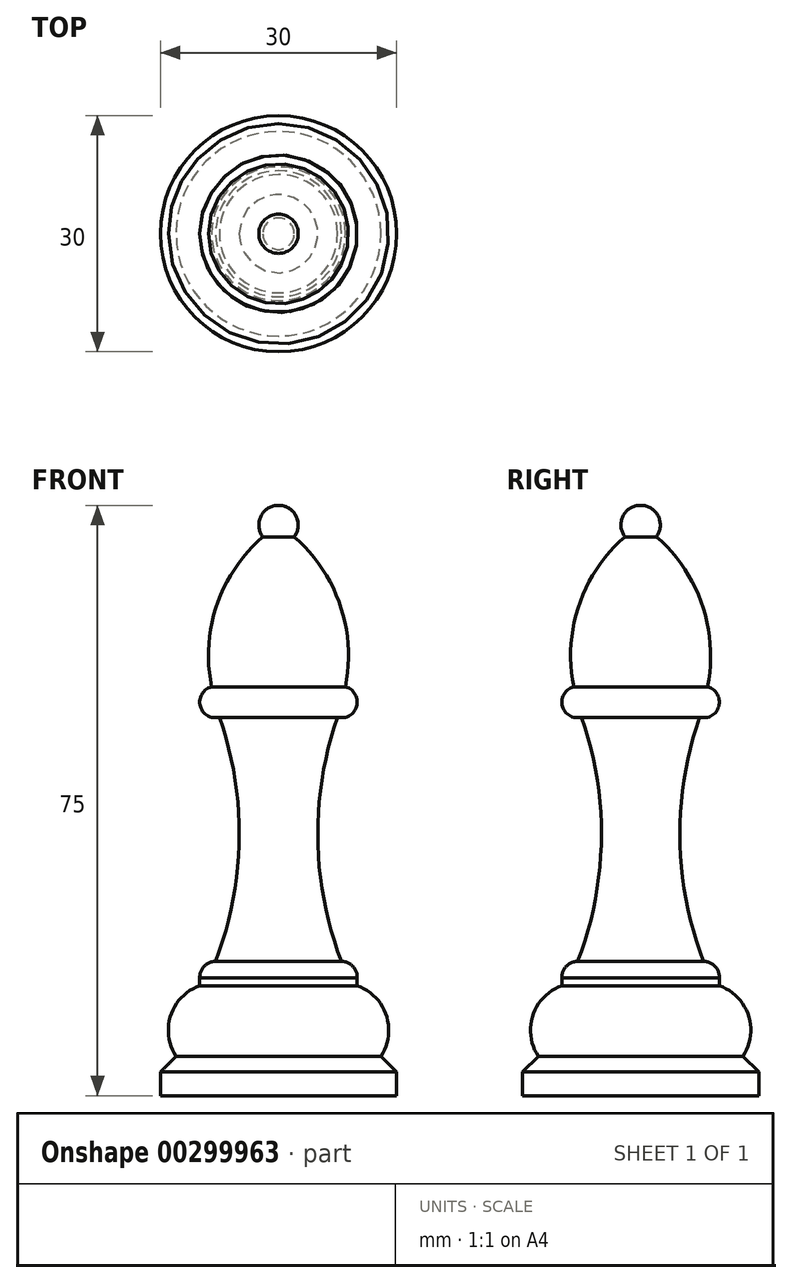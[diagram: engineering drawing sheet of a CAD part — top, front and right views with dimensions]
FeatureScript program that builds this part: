
annotation { "Feature Type Name" : "Feature", "Feature Type Description" : "" }
export const myFeature = defineFeature(function(context is Context, id is Id, definition is map)
    precondition{}
    {
        {
            var Q0;
            Q0=qCreatedBy(makeId("Front.planeOp"),FACE);
            var sketch = newSketch(context, id + "F0", { "sketchPlane" : qUnion([Q0])});
            skArc(sketch, "E0", {"start": v(2, -4) * mm, "mid": v(2.24, -1.38) * mm, "end": v(0, 0) * mm});
            skArc(sketch, "E1", {"start": v(8.5, -23.06) * mm, "mid": v(7.82, -12.65) * mm, "end": v(2, -4) * mm});
            skArc(sketch, "E2", {"start": v(8.5, -26.93) * mm, "mid": v(10, -25) * mm, "end": v(8.5, -23.06) * mm});
            skLineSegment(sketch, "E3", {"start": v(8.5, -26.93) * mm, "end": v(7.5, -26.93) * mm});
            skArc(sketch, "E4", {"start": v(7.5, -26.93) * mm, "mid": v(5, -42.49) * mm, "end": v(8, -57.95) * mm});
            skArc(sketch, "E5", {"start": v(10, -60.03) * mm, "mid": v(9.44, -58.57) * mm, "end": v(8, -57.95) * mm});
            skLineSegment(sketch, "E6", {"start": v(10, -60.03) * mm, "end": v(10, -61.03) * mm});
            skLineSegment(sketch, "E7", {"start": v(13, -70) * mm, "end": v(15, -72) * mm});
            skLineSegment(sketch, "E8", {"start": v(15, -72) * mm, "end": v(15, -75) * mm});
            skLineSegment(sketch, "E9", {"start": v(15, -75) * mm, "end": v(0, -75) * mm});
            skLineSegment(sketch, "E10", {"start": v(0, -75) * mm, "end": v(0, 0) * mm});
            skArc(sketch, "E11", {"start": v(13, -70) * mm, "mid": v(13.69, -64.78) * mm, "end": v(10, -61.03) * mm});
            skSolve(sketch);
        }
        {
            var Q0;
            Q0=makeQuery(id+"F0.imprint","IMPRINT",FACE,{"disambiguationData":[TD([[makeQuery(id+"F0.imprint","IMPRINT",EDGE,{"derivedFrom":sQuery(id+"F0.wireOp",EDGE,"E0")}),1.0]])]});
            var Q1;
            Q1=sQuery(id+"F0.wireOp",EDGE,"E10");
            revolve(context, id + "F1", {"entities" : qUnion([Q0]), "axis" : qUnion([Q1]), "revolveType" : RevolveType.FULL});
        }
    });
